# Revit family: J2 PET Felt Box Baffle
name_source: partatom
category: Specialty Equipment
units: mm (PartAtom-declared; Revit-internal decimal feet)

## family parameters
Always vertical = Yes
Cut with Voids When Loaded = No
Part Type = Normal
Room Calculation Point = No
Round Connector Dimension = Use Diameter
Shared = No
Work Plane-Based = No

## types (3) — shared parameters
Baffle Height (Max. 3'-11") = 0' - 7 3/4"
Baffle Width (Max. 4") = 0' - 2"
Default Elevation = 0' - 0"
Felt Color - Accent = <By Category>
Felt Color - Primary = <By Category>
Manufacturer = J2 Systems
Product Line = Ceiling System
Release Date = 2021
URL = https://www.j2systems.net

## per-type parameters (varying)
| type | Baffle Length (Max. 7'-11") | Model | Style Number |
| Box Baffle 8ft | 7' - 11" | Box Baffle 8ft | CSBB08 |
| Box Baffle 6ft | 5' - 11" | Box Baffle 6ft | CSBB06 |
| Box Baffle 4ft | 3' - 11" | Box Baffle 6ft | CSBB04 |

## geometry (parser evidence)
native form markers: Blend x4, Sweep x2
no freeform markers — native parametric forms only
